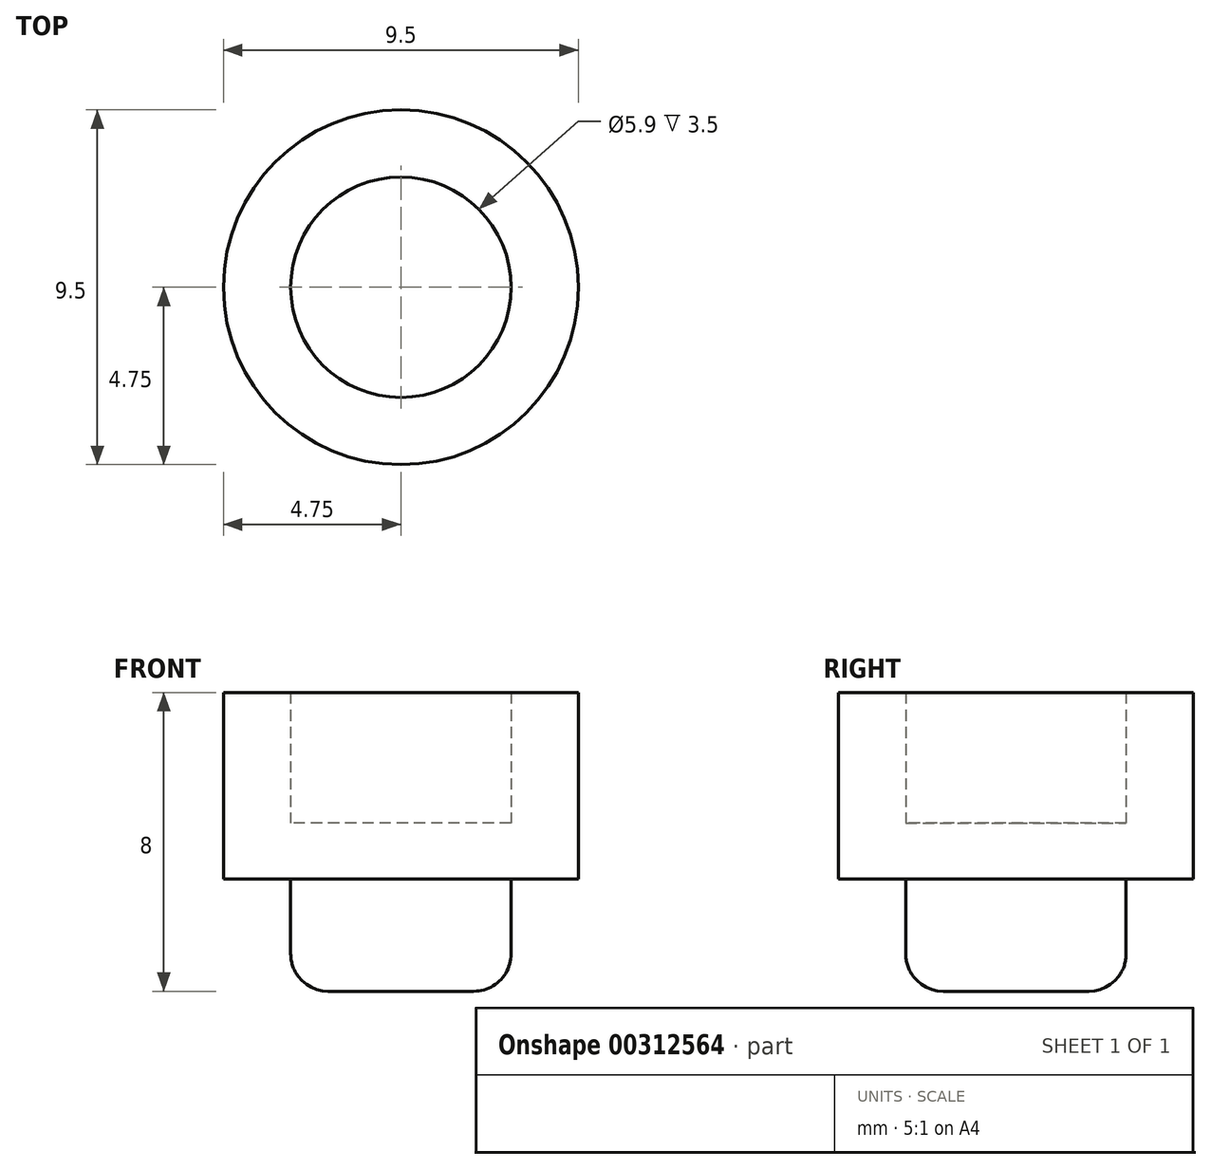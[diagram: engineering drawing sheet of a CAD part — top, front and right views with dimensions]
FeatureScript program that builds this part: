
annotation { "Feature Type Name" : "Feature", "Feature Type Description" : "" }
export const myFeature = defineFeature(function(context is Context, id is Id, definition is map)
    precondition{}
    {
        {
            var Q0;
            Q0=qCreatedBy(makeId("Top.planeOp"),FACE);
            var sketch = newSketch(context, id + "F0", { "sketchPlane" : qUnion([Q0])});
            skCircle(sketch, "E0", {"center": v(0, 0) * mm, "radius": 2.95 * mm});
            skCircle(sketch, "E1", {"center": v(0, 0) * mm, "radius": 4.75 * mm});
            skSolve(sketch);
        }
        {
            var Q0;
            Q0=makeQuery(id+"F0.imprint","IMPRINT",FACE,{"disambiguationData":[TD([[makeQuery(id+"F0.imprint","IMPRINT",EDGE,{"derivedFrom":sQuery(id+"F0.wireOp",EDGE,"E0")}),-1.0]])]});
            extrude(context, id + "F1", {"entities" : qUnion([Q0]), "depth" : 5 * mm});
        }
        {
            var Q0;
            Q0=makeQuery(id+"F0.imprint","IMPRINT",FACE,{"disambiguationData":[TD([[makeQuery(id+"F0.imprint","IMPRINT",EDGE,{"derivedFrom":sQuery(id+"F0.wireOp",EDGE,"E0")}),1.0]])]});
            extrude(context, id + "F2", {"entities" : qUnion([Q0]), "operationType" : NewBodyOperationType.ADD, "oppositeDirection" : true, "depth" : 3 * mm, "hasSecondDirection" : true, "secondDirectionOppositeDirection" : false, "secondDirectionDepth" : 1.5 * mm});
        }
        {
            var Q0;
            Q0=makeQuery(id+"F2.opExtrude","CAP_EDGE",EDGE,{"disambiguationData":[OSD([sQuery(id+"F0.wireOp",EDGE,"E0")])],"isStart":false});
            fillet(context, id + "F3", {"entities" : qUnion([Q0]), "radius" : 1 * mm, "tangentPropagation" : true, "allowEdgeOverflow" : false});
        }
    });
